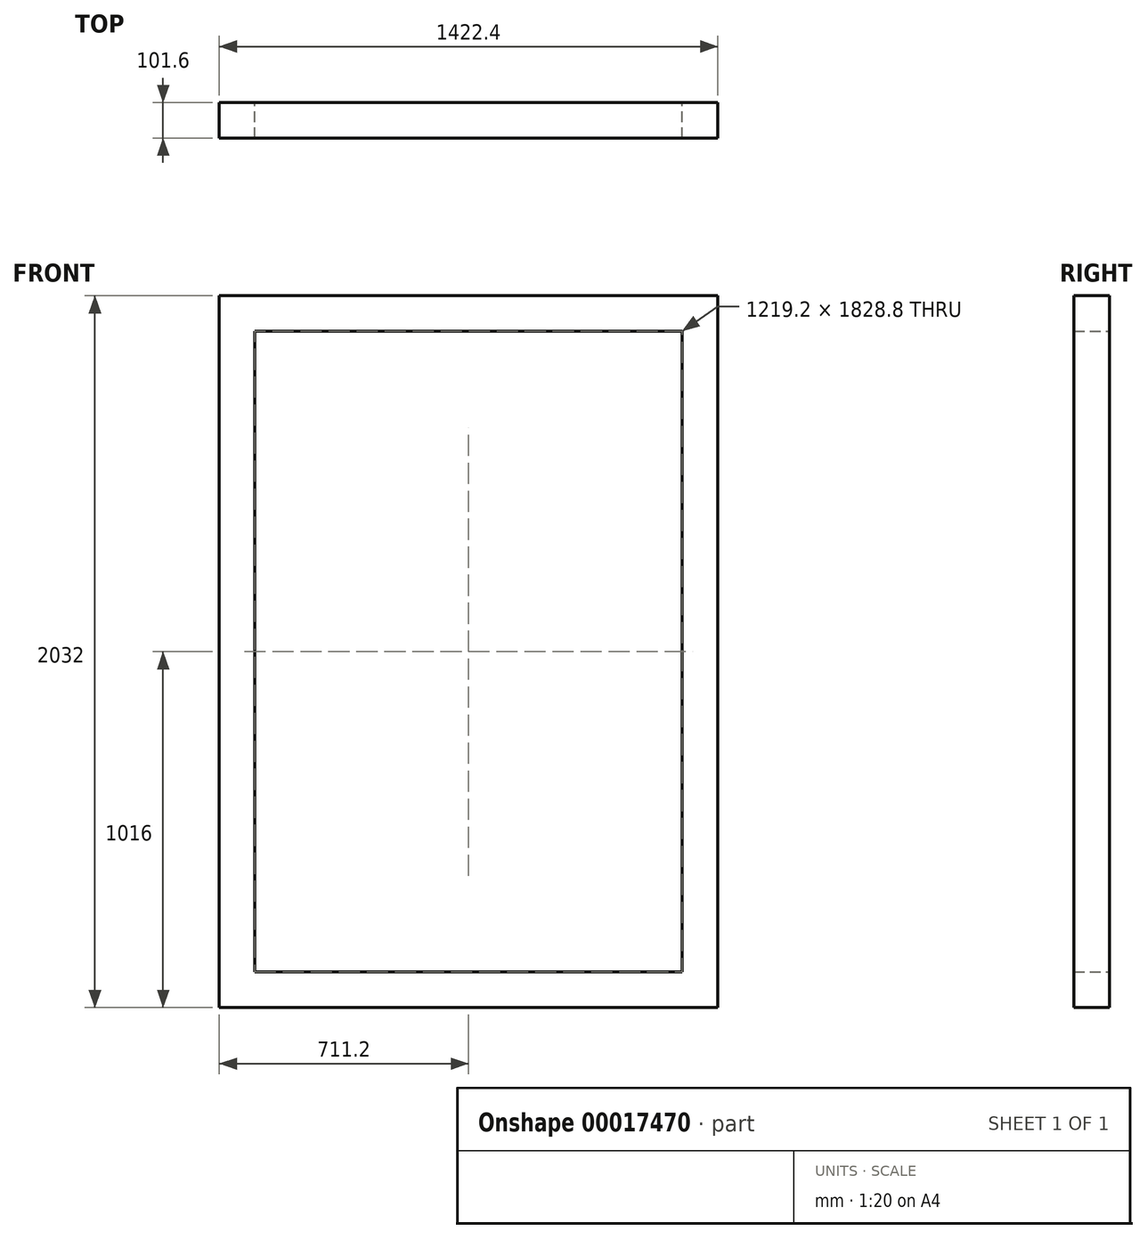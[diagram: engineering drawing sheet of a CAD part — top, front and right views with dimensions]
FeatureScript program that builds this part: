
annotation { "Feature Type Name" : "Feature", "Feature Type Description" : "" }
export const myFeature = defineFeature(function(context is Context, id is Id, definition is map)
    precondition{}
    {
        {
            var Q0;
            Q0=qCreatedBy(makeId("Front.planeOp"),FACE);
            var sketch = newSketch(context, id + "F0", { "sketchPlane" : qUnion([Q0])});
            skLineSegment(sketch, "E0.bottom", {"start": v(-711.2, 1016) * mm, "end": v(711.2, 1016) * mm});
            skLineSegment(sketch, "E0.top", {"start": v(-711.2, -1016) * mm, "end": v(711.2, -1016) * mm});
            skLineSegment(sketch, "E0.left", {"start": v(-711.2, 1016) * mm, "end": v(-711.2, -1016) * mm});
            skLineSegment(sketch, "E0.right", {"start": v(711.2, 1016) * mm, "end": v(711.2, -1016) * mm});
            skLineSegment(sketch, "E1.bottom", {"start": v(-609.6, 914.4) * mm, "end": v(609.6, 914.4) * mm});
            skLineSegment(sketch, "E1.top", {"start": v(-609.6, -914.4) * mm, "end": v(609.6, -914.4) * mm});
            skLineSegment(sketch, "E1.left", {"start": v(-609.6, 914.4) * mm, "end": v(-609.6, -914.4) * mm});
            skLineSegment(sketch, "E1.right", {"start": v(609.6, 914.4) * mm, "end": v(609.6, -914.4) * mm});
            skSolve(sketch);
        }
        {
            var Q0;
            Q0 = qSketchRegion(id + "F0", true);
            extrude(context, id + "F1", {"entities" : qUnion([Q0]), "endBound" : BoundingType.SYMMETRIC, "depth" : 101.6 * mm});
        }
    });
